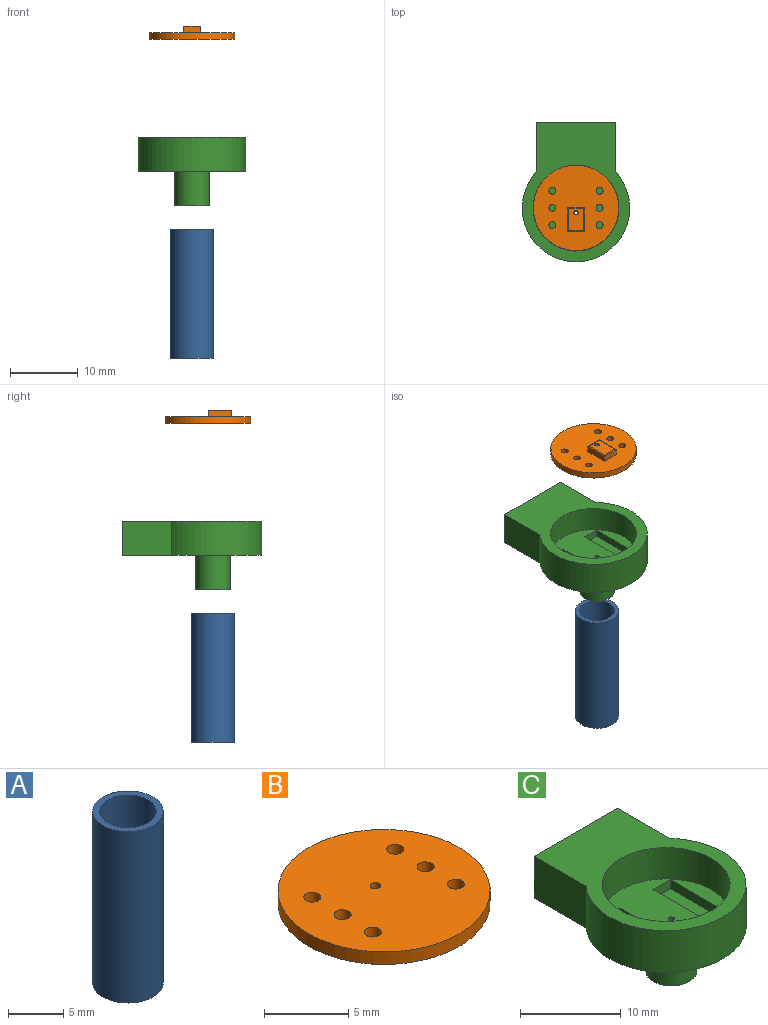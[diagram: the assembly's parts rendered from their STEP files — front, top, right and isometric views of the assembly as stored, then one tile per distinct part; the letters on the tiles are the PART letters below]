
ASSEMBLY  parts=3 mates=2
PART A: 4 faces, bbox 6.4x6.4x19.1 mm
  f0: cylinder r=2.57mm len=19.05mm, axis (0,0,-1), area 307.1mm2, adj f2,f3
  f1: cylinder r=3.2mm len=19.05mm, axis (0,0,-1), area 383.1mm2, adj f2,f3
  f2: plane 6.4x6.4mm, normal (0,0,1), area 11.5mm2, adj f0,f1
  f3: plane 6.4x6.4mm, normal (0,0,-1), area 11.5mm2, adj f0,f1
PART B: 19 faces, bbox 12.6x12.6x1.9 mm
  f0: cylinder r=0.32mm len=1.93mm, axis (0,0,-1), area 3.9mm2, adj f2,f8
  f1: cylinder r=6.31mm len=12.62mm, axis (0,0,-1), area 36.3mm2, adj f2,f3
  f2: plane 12.62x12.62mm, normal (0,0,1), area 120mm2, adj f0,f1,f13,f14,f15,f16,f17,f18
  f3: plane 12.62x12.62mm, normal (0,0,-1), area 111.8mm2, adj f1,f4,f5,f6,f7,f13,f14,f15
  f4: plane 2.41x0.89mm, normal (0,1,0), area 2.1mm2, adj f3,f5,f7,f11
  f5: plane 3.51x0.89mm, normal (1,0,0), area 3.1mm2, adj f3,f4,f6,f9
  f6: plane 2.41x0.89mm, normal (0,-1,0), area 2.1mm2, adj f3,f5,f7,f10
  f7: plane 3.51x0.89mm, normal (-1,0,0), area 3.1mm2, adj f3,f4,f6,f12
  f8: plane 3.25x2.16mm, normal (0,0,-1), area 6.7mm2, adj f0,f9,f10,f11,f12
  f9: cylinder r=0.13mm len=3.51mm, axis (0,1,0), area 0.7mm2, adj f5,f8,f10,f11
  f10: cylinder r=0.13mm len=2.41mm, axis (1,0,0), area 0.5mm2, adj f6,f8,f9,f12
  f11: cylinder r=0.13mm len=2.41mm, axis (-1,0,0), area 0.5mm2, adj f4,f8,f9,f12
  f12: cylinder r=0.13mm len=3.51mm, axis (0,-1,0), area 0.7mm2, adj f7,f8,f10,f11
  f13: cylinder r=0.51mm len=1.02mm, axis (0,0,1), area 2.9mm2, adj f2,f3
  f14: cylinder r=0.51mm len=1.02mm, axis (0,0,1), area 2.9mm2, adj f2,f3
  f15: cylinder r=0.51mm len=1.02mm, axis (0,0,1), area 2.9mm2, adj f2,f3
  f16: cylinder r=0.51mm len=1.02mm, axis (0,0,1), area 2.9mm2, adj f2,f3
  f17: cylinder r=0.51mm len=1.02mm, axis (0,0,1), area 2.9mm2, adj f2,f3
  f18: cylinder r=0.51mm len=1.02mm, axis (0,0,1), area 2.9mm2, adj f2,f3
PART C: 23 faces, bbox 15.9x20.6x10.2 mm
  f0: cylinder r=7.94mm len=15.88mm, axis (0,0,-1), area 186.5mm2, adj f3,f4,f20,f22
  f1: cylinder r=0.32mm len=1.27mm, axis (0,0,-1), area 2.5mm2, adj f2,f19
  f2: plane 12.7x12.7mm, normal (0,0,1), area 86.1mm2, adj f1,f5,f6,f7,f8,f9,f11,f12
  f3: plane 20.64x15.88mm, normal (0,0,1), area 136.3mm2, adj f0,f5,f20,f21,f22
  f4: plane 20.64x15.88mm, normal (0,0,-1), area 242.7mm2, adj f0,f16,f20,f21,f22
  f5: cylinder r=6.35mm len=12.7mm, axis (0,0,1), area 152mm2, adj f2,f3
  f6: plane 8.25x1.12mm, normal (1,0,0), area 9.2mm2, adj f2,f7,f9,f10
  f7: plane 2.44x1.12mm, normal (0,1,0), area 2.7mm2, adj f2,f6,f8,f10
  f8: plane 8.25x1.12mm, normal (-1,0,0), area 9.2mm2, adj f2,f7,f9,f10
  f9: plane 2.44x1.12mm, normal (0,-1,0), area 2.7mm2, adj f2,f6,f8,f10
  f10: plane 8.25x2.44mm, normal (0,0,1), area 20.1mm2, adj f6,f7,f8,f9
  f11: plane 2.44x1.12mm, normal (0,1,0), area 2.7mm2, adj f2,f12,f14,f15
  f12: plane 8.25x1.12mm, normal (-1,0,0), area 9.2mm2, adj f2,f11,f13,f15
  f13: plane 2.44x1.12mm, normal (0,-1,0), area 2.7mm2, adj f2,f12,f14,f15
  f14: plane 8.25x1.12mm, normal (1,0,0), area 9.2mm2, adj f2,f11,f13,f15
  f15: plane 8.25x2.44mm, normal (0,0,1), area 20.1mm2, adj f11,f12,f13,f14
  f16: cylinder r=2.54mm len=5.08mm, axis (0,0,1), area 81.1mm2, adj f4,f17
  f17: plane 5.08x5.08mm, normal (0,0,-1), area 8.9mm2, adj f16,f18
  f18: cylinder r=1.91mm len=5.08mm, axis (0,0,-1), area 60.8mm2, adj f17,f19
  f19: plane 3.81x3.81mm, normal (0,0,-1), area 11.1mm2, adj f1,f18
  f20: plane 7.34x5.08mm, normal (1,0,0), area 37.3mm2, adj f0,f3,f4,f21
  f21: plane 11.7x5.08mm, normal (0,1,0), area 59.4mm2, adj f3,f4,f20,f22
  f22: plane 7.34x5.08mm, normal (-1,0,0), area 37.3mm2, adj f0,f3,f4,f21
PLACE A t=(0,-0.72,-27.57)mm
PLACE B rot(axis=(1,0,0),180deg) t=(0,0,20.47)mm
PLACE C at identity fixed
MATE slider B.f0 <-> C.f1  axis (0,0,-1) through (0,-0.72,19.56)mm
MATE slider A.f0 <-> C.f16  axis (0,0,1) through (0,-0.72,-8.52)mm
